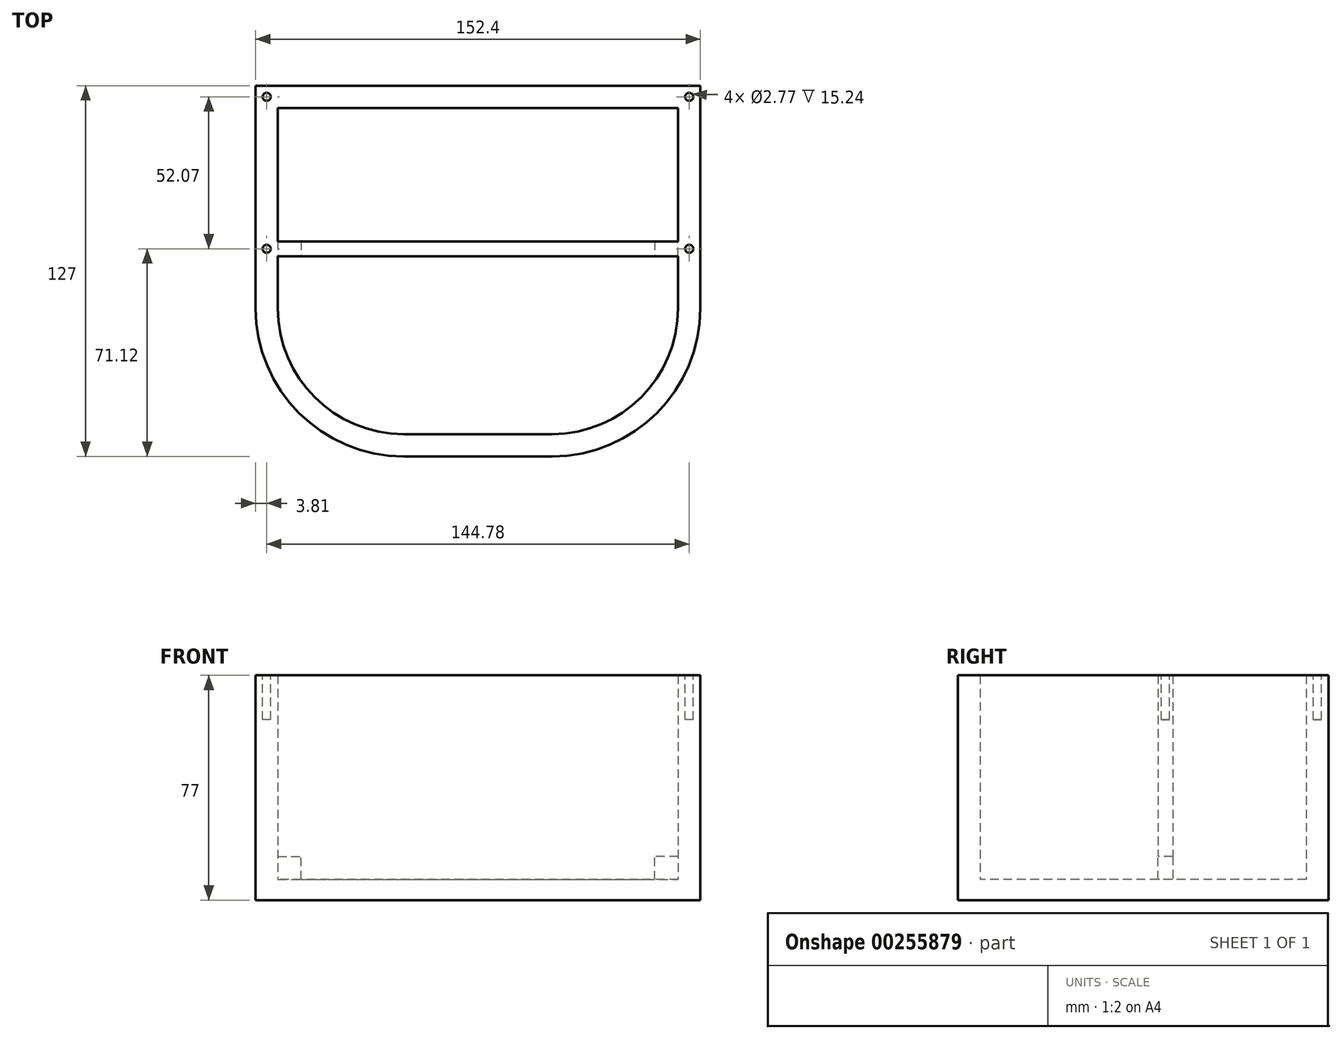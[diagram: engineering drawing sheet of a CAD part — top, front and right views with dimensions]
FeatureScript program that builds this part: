
annotation { "Feature Type Name" : "Feature", "Feature Type Description" : "" }
export const myFeature = defineFeature(function(context is Context, id is Id, definition is map)
    precondition{}
    {
        {
            var Q0;
            Q0=qCreatedBy(makeId("Top.planeOp"),FACE);
            var sketch = newSketch(context, id + "F0", { "sketchPlane" : qUnion([Q0])});
            skLineSegment(sketch, "E0.bottom", {"start": v(0, 0) * mm, "end": v(152.4, 0) * mm});
            skLineSegment(sketch, "E0.top", {"start": v(50.8, -127) * mm, "end": v(101.6, -127) * mm});
            skLineSegment(sketch, "E0.left", {"start": v(0, 0) * mm, "end": v(0, -76.2) * mm});
            skLineSegment(sketch, "E0.right", {"start": v(152.4, 0) * mm, "end": v(152.4, -76.2) * mm});
            skPoint(sketch, "E1.visualSharp", {"position": v(0, -127) * mm});
            skArc(sketch, "E1.filletArc", {"start": v(0, -76.2) * mm, "mid": v(14.88, -112.12) * mm, "end": v(50.8, -127) * mm});
            skPoint(sketch, "E2.visualSharp", {"position": v(152.4, -127) * mm});
            skArc(sketch, "E2.filletArc", {"start": v(101.6, -127) * mm, "mid": v(137.52, -112.12) * mm, "end": v(152.4, -76.2) * mm});
            skSolve(sketch);
        }
        {
            var Q0;
            Q0 = qSketchRegion(id + "F0", true);
            extrude(context, id + "F1", {"entities" : qUnion([Q0]), "depth" : 7 * mm});
        }
        {
            var Q0;
            Q0=makeQuery(id+"F1.opExtrude","CAP_FACE",FACE,{"disambiguationData":[OSD([sQuery(id+"F0.wireOp",EDGE,"E0.bottom"),sQuery(id+"F0.wireOp",EDGE,"E0.top"),sQuery(id+"F0.wireOp",EDGE,"E0.left"),sQuery(id+"F0.wireOp",EDGE,"E0.right"),sQuery(id+"F0.wireOp",EDGE,"E1.filletArc"),sQuery(id+"F0.wireOp",EDGE,"E2.filletArc")])],"isStart":false});
            var sketch = newSketch(context, id + "F2", { "sketchPlane" : qUnion([Q0])});
            skLineSegment(sketch, "E3", {"start": v(76.2, 0) * mm, "end": v(76.2, -127) * mm, "construction": true});
            skLineSegment(sketch, "E4.bottom", {"start": v(38.97, -9.85) * mm, "end": v(108.97, -9.85) * mm, "construction": true});
            skLineSegment(sketch, "E4.top", {"start": v(38.97, -49.85) * mm, "end": v(108.97, -49.85) * mm, "construction": true});
            skLineSegment(sketch, "E4.left", {"start": v(38.97, -9.85) * mm, "end": v(38.97, -49.85) * mm, "construction": true});
            skLineSegment(sketch, "E4.right", {"start": v(108.97, -9.85) * mm, "end": v(108.97, -49.85) * mm, "construction": true});
            skLineSegment(sketch, "E5", {"start": v(0, 0) * mm, "end": v(152.4, 0) * mm});
            skLineSegment(sketch, "E6", {"start": v(152.4, 0) * mm, "end": v(152.4, -76.2) * mm});
            skLineSegment(sketch, "E7", {"start": v(101.6, -127) * mm, "end": v(50.8, -127) * mm});
            skLineSegment(sketch, "E8", {"start": v(0, -76.2) * mm, "end": v(0, 0) * mm});
            skPoint(sketch, "E9.visualSharp", {"position": v(0, -127) * mm});
            skArc(sketch, "E9.filletArc", {"start": v(0, -76.2) * mm, "mid": v(14.88, -112.12) * mm, "end": v(50.8, -127) * mm});
            skPoint(sketch, "E10.visualSharp", {"position": v(152.4, -127) * mm});
            skArc(sketch, "E10.filletArc", {"start": v(101.6, -127) * mm, "mid": v(137.52, -112.12) * mm, "end": v(152.4, -76.2) * mm});
            skLineSegment(sketch, "E11.0", {"start": v(7.62, -7.62) * mm, "end": v(7.62, -76.2) * mm});
            skLineSegment(sketch, "E11.1", {"start": v(50.8, -119.38) * mm, "end": v(101.6, -119.38) * mm});
            skArc(sketch, "E11.2", {"start": v(101.6, -119.38) * mm, "mid": v(132.13, -106.73) * mm, "end": v(144.78, -76.2) * mm});
            skArc(sketch, "E11.3", {"start": v(7.62, -76.2) * mm, "mid": v(20.27, -106.73) * mm, "end": v(50.8, -119.38) * mm});
            skLineSegment(sketch, "E11.4", {"start": v(144.78, -76.2) * mm, "end": v(144.78, -7.62) * mm});
            skLineSegment(sketch, "E11.5", {"start": v(144.78, -7.62) * mm, "end": v(7.62, -7.62) * mm});
            skLineSegment(sketch, "E12.bottom", {"start": v(7.62, -53.34) * mm, "end": v(144.78, -53.34) * mm});
            skLineSegment(sketch, "E12.top", {"start": v(7.62, -58.42) * mm, "end": v(144.78, -58.42) * mm});
            skLineSegment(sketch, "E12.left", {"start": v(7.62, -53.34) * mm, "end": v(7.62, -58.42) * mm});
            skLineSegment(sketch, "E12.right", {"start": v(144.78, -53.34) * mm, "end": v(144.78, -58.42) * mm});
            skSolve(sketch);
        }
        {
            var Q0;
            Q0 = qSketchRegion(id + "F2", true);
            var Q1;
            Q1=makeQuery(id+"F2.imprint","IMPRINT",FACE,{"disambiguationData":[TD([[makeQuery(id+"F2.imprint","IMPRINT",EDGE,{"derivedFrom":sQuery(id+"F2.wireOp",EDGE,"E12.bottom")}),-1.0]])]});
            extrude(context, id + "F3", {"entities" : qUnion([Q0, Q1]), "operationType" : NewBodyOperationType.ADD, "depth" : 100 * mm});
        }
        {
            var Q0;
            Q0=makeQuery(id+"F3.opExtrude","CAP_FACE",FACE,{"disambiguationData":[OSD([sQuery(id+"F2.wireOp",EDGE,"E5"),sQuery(id+"F2.wireOp",EDGE,"E6"),sQuery(id+"F2.wireOp",EDGE,"E7"),sQuery(id+"F2.wireOp",EDGE,"E8"),sQuery(id+"F2.wireOp",EDGE,"E9.filletArc"),sQuery(id+"F2.wireOp",EDGE,"E10.filletArc"),sQuery(id+"F2.wireOp",EDGE,"E11.0"),sQuery(id+"F2.wireOp",EDGE,"E11.1"),sQuery(id+"F2.wireOp",EDGE,"E11.2"),sQuery(id+"F2.wireOp",EDGE,"E11.3"),sQuery(id+"F2.wireOp",EDGE,"E11.4"),sQuery(id+"F2.wireOp",EDGE,"E11.5"),sQuery(id+"F2.wireOp",EDGE,"E12.bottom"),sQuery(id+"F2.wireOp",EDGE,"E12.top")])],"isStart":false});
            var sketch = newSketch(context, id + "F4", { "sketchPlane" : qUnion([Q0])});
            skLineSegment(sketch, "E13", {"start": v(0, -58.42) * mm, "end": v(0, -127) * mm});
            skLineSegment(sketch, "E14", {"start": v(0, -127) * mm, "end": v(152.4, -127) * mm});
            skLineSegment(sketch, "E15", {"start": v(152.4, -127) * mm, "end": v(152.4, -58.42) * mm});
            skLineSegment(sketch, "E16", {"start": v(0, -58.42) * mm, "end": v(0, 0) * mm});
            skLineSegment(sketch, "E17", {"start": v(0, 0) * mm, "end": v(152.4, 0) * mm});
            skLineSegment(sketch, "E18", {"start": v(152.4, 0) * mm, "end": v(152.4, -58.42) * mm});
            skSolve(sketch);
        }
        {
            var Q0;
            Q0 = qSketchRegion(id + "F4", true);
            extrude(context, id + "F5", {"entities" : qUnion([Q0]), "operationType" : NewBodyOperationType.REMOVE, "oppositeDirection" : true, "depth" : 30 * mm});
        }
        {
            var Q0;
            Q0=makeQuery(id+"F3.opExtrude","SWEPT_FACE",FACE,{"disambiguationData":[OSD([sQuery(id+"F2.wireOp",EDGE,"E12.top")])]});
            var sketch = newSketch(context, id + "F6", { "sketchPlane" : qUnion([Q0])});
            skLineSegment(sketch, "E19.bottom", {"start": v(7.62, 7) * mm, "end": v(15.62, 7) * mm});
            skLineSegment(sketch, "E19.top", {"start": v(7.62, 15) * mm, "end": v(15.62, 15) * mm});
            skLineSegment(sketch, "E19.left", {"start": v(7.62, 7) * mm, "end": v(7.62, 15) * mm});
            skLineSegment(sketch, "E19.right", {"start": v(15.62, 7) * mm, "end": v(15.62, 15) * mm});
            skLineSegment(sketch, "E20.bottom", {"start": v(144.78, 7) * mm, "end": v(136.78, 7) * mm});
            skLineSegment(sketch, "E20.top", {"start": v(144.78, 15) * mm, "end": v(136.78, 15) * mm});
            skLineSegment(sketch, "E20.left", {"start": v(144.78, 7) * mm, "end": v(144.78, 15) * mm});
            skLineSegment(sketch, "E20.right", {"start": v(136.78, 7) * mm, "end": v(136.78, 15) * mm});
            skSolve(sketch);
        }
        {
            var Q0;
            Q0 = qSketchRegion(id + "F6", true);
            extrude(context, id + "F7", {"entities" : qUnion([Q0]), "operationType" : NewBodyOperationType.REMOVE, "oppositeDirection" : true, "depth" : 25.4 * mm});
        }
        {
            var Q0;
            Q0=makeQuery(id+"F5.boolean.opBoolean","COPY",FACE,{"derivedFrom":makeQuery(id+"F5.opExtrude","CAP_FACE",FACE,{"disambiguationData":[OSD([sQuery(id+"F4.wireOp",EDGE,"E13"),sQuery(id+"F4.wireOp",EDGE,"E14"),sQuery(id+"F4.wireOp",EDGE,"E15"),sQuery(id+"F4.wireOp",EDGE,"E16"),sQuery(id+"F4.wireOp",EDGE,"E17"),sQuery(id+"F4.wireOp",EDGE,"E18")])],"isStart":false})});
            var sketch = newSketch(context, id + "F8", { "sketchPlane" : qUnion([Q0])});
            skCircle(sketch, "E21", {"center": v(3.81, -3.8) * mm, "radius": 1.38 * mm});
            skCircle(sketch, "E22", {"center": v(3.81, -55.88) * mm, "radius": 1.38 * mm});
            skLineSegment(sketch, "E23", {"start": v(76.2, -7.62) * mm, "end": v(76.2, -13.46) * mm, "construction": true});
            skCircle(sketch, "E24.MirrorC", {"center": v(148.6, -3.8) * mm, "radius": 1.38 * mm});
            skCircle(sketch, "E25.MirrorC", {"center": v(148.6, -55.88) * mm, "radius": 1.38 * mm});
            skSolve(sketch);
        }
        {
            var Q0;
            Q0 = qSketchRegion(id + "F8", true);
            extrude(context, id + "F9", {"entities" : qUnion([Q0]), "operationType" : NewBodyOperationType.REMOVE, "oppositeDirection" : true, "depth" : 15.24 * mm});
        }
    });
